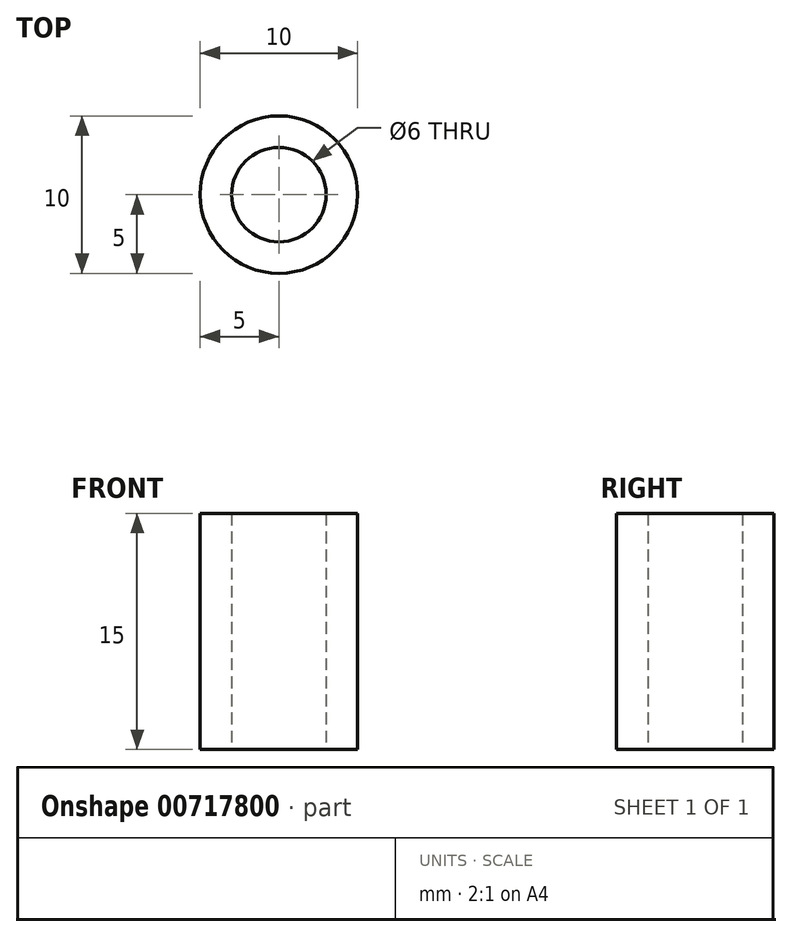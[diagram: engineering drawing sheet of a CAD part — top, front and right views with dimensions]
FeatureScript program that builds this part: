
annotation { "Feature Type Name" : "Feature", "Feature Type Description" : "" }
export const myFeature = defineFeature(function(context is Context, id is Id, definition is map)
    precondition{}
    {
        {
            var Q0;
            Q0=qCreatedBy(makeId("Top.planeOp"),FACE);
            var sketch = newSketch(context, id + "F0", { "sketchPlane" : qUnion([Q0])});
            skCircle(sketch, "E0", {"center": v(0, 0) * mm, "radius": 5 * mm});
            skCircle(sketch, "E1", {"center": v(0, 0) * mm, "radius": 3 * mm});
            skSolve(sketch);
        }
        {
            var Q0;
            Q0 = qSketchRegion(id + "F0", true);
            extrude(context, id + "F1", {"entities" : qUnion([Q0]), "depth" : 15 * mm, "offsetDistance" : 25 * mm});
        }
    });
